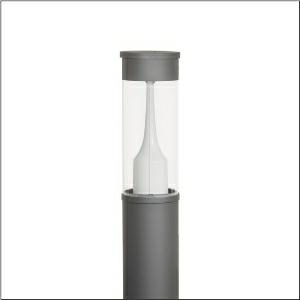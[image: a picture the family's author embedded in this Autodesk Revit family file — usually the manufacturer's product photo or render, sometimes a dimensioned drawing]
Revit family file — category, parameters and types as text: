
# Revit family: city-light_260_iq___st1_2a_5xa5295ef14h_2f06
name_source: partatom
category: Lighting Fixtures
units: mm (PartAtom-declared; Revit-internal decimal feet)

## family parameters
Cut with Voids When Loaded = No
Host = Face
Light Source = No
Part Type = Normal
Room Calculation Point = No
Round Connector Dimension = Use Diameter
Shared = No

## types (1)
- --- (1 x LED, 1540 lm, 10.5 W, 3000K)
    Apparent Load = 11 VA
    CIE Flux Codes = 22 61 93 96 100
    Color Rendering = 70
    Color Temperature = 3000K
    Default Elevation = 1800 mm
    Description = City-Light 260 iQ, light pillar, Module 540 iQ-SR, primary light control with 3 zone facetted reflector, of plastic, silver coated, highly specular, structured, primary optical cover: cover, of PMMA, transparent, light distribution: ST1.2a, primary light characteristic: asymmetric, LED, High Power LED, rated luminous flux: 1.540lm, luminous efficacy: 147lm/W, light colour: 730, colour temperature: 3000K, control gear: iQ Street-Remote, control: Auto-Match, Temp-Guard, Lumen-Switch, Night-Set, Smart-Wire, Light-Fading, Desk-Remote (wireless, voltage-free reading and setting of iQ features in the workshop via application-optimized NFC function/RFID function), optimised constant luminous flux control (CLO 2.0), Street-Remote, pre-setting: logarithmic dimming characteristic, with terminal, 6-pole, max. 2.5mm², mains connection: 230..240V, AC, 50/60Hz, start of lifetime: 11W, end of service life: 11W, reduction: 5W, luminaire housing, cylindrical, of extruded aluminium section, coated, Siteco® metallic grey (DB 702S), length: 2.600mm, diameter: 200mm, Module 540 iQ-SR, traffic white (RAL 9016), equipment: standard, protection rating (complete): IP65, insulation class (complete): insulation class II (safety insulation), certification: CE, ENEC, VDE, packaging unit: 1 piece

Light Distribution: ST1.2a
    Height = 500 mm
    Lamp = 1 x LED
    Lamp Light Flux = 1540 lm
    Lamp Power = 10.5 W
    Lamp count = 1
    Length = 200 mm  [stored 0.656168 ft]
    Luminous efficacy = 147 lm/W
    Manufacturer = Siteco
    ModVariant = No
    Model = 5XA5295EF14H
    Mounting Place = Floor
    Mounting Type = Freestanding
    Number of Poles = 1
    OnlyDefault = Yes
    Power Factor = 1
    Product Name = City-Light 260 iQ | ST1.2a
    Product group = light pillar
    ProductGroupID = 1301
    Protection Class = Protection class II
    Protection Degree = IP 65
    RLX_Detail_Level = 1
    RLX_Emergency_Light_Flux = 0 lm
    RLX_Emergency_Type = 0
    RLX_Emergency_Type_DB = No
    RlxData = <blob elided: 60757 chars, md5=12f83dfa>
    Socket = socket
    Standby Power = 0 W
    System Light Flux = 1540 lm
    System Power = 11 W
    Type Comments = factory setting: luminous flux: 100 % | dim-lin: 254 | 419 mA
    Type Image = l_1006918.jpg
    URL = http://relux.com
    VarID = @adj_180669
    Voltage = 0 V
    Weight = 0.00 kg
    Width = 0 mm  [stored 0 ft]

note: [stored X ft] marks values corroborated as IEEE doubles in the binary element streams (Revit-internal decimal feet)

## geometry (parser evidence)
native form markers: Blend x4, Sweep x12
no freeform markers — native parametric forms only
